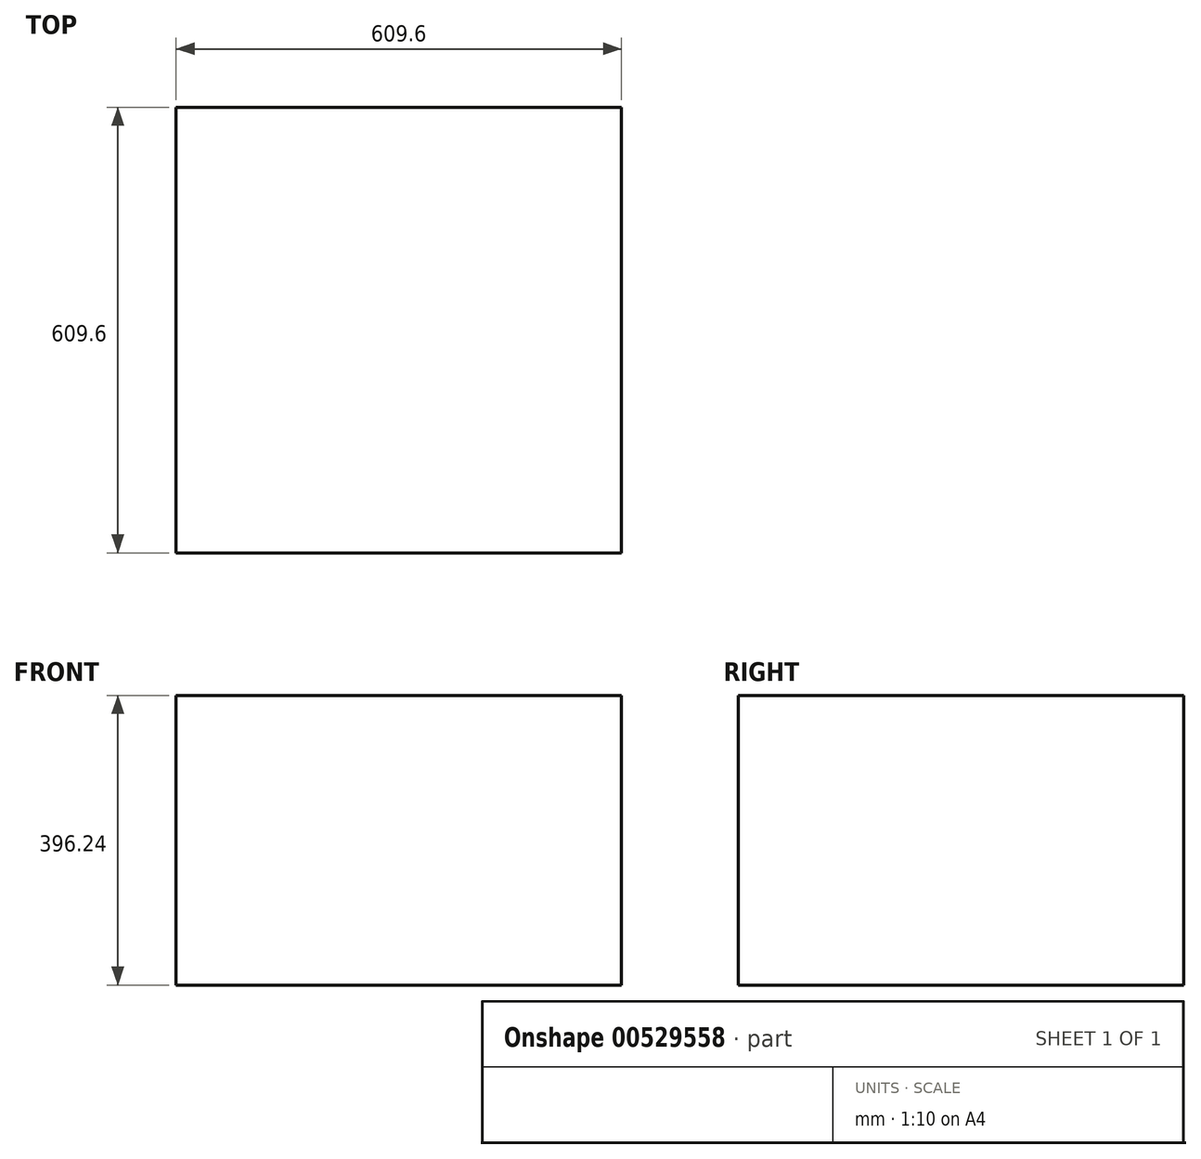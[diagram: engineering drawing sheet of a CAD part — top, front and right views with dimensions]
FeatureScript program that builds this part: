
annotation { "Feature Type Name" : "Feature", "Feature Type Description" : "" }
export const myFeature = defineFeature(function(context is Context, id is Id, definition is map)
    precondition{}
    {
        {
            var Q0;
            Q0=qCreatedBy(makeId("Top.planeOp"),FACE);
            var sketch = newSketch(context, id + "F0", { "sketchPlane" : qUnion([Q0])});
            skLineSegment(sketch, "E0.bottom", {"start": v(-304, 233.03) * mm, "end": v(305.6, 233.03) * mm});
            skLineSegment(sketch, "E0.top", {"start": v(-304, -376.57) * mm, "end": v(305.6, -376.57) * mm});
            skLineSegment(sketch, "E0.left", {"start": v(-304, 233.03) * mm, "end": v(-304, -376.57) * mm});
            skLineSegment(sketch, "E0.right", {"start": v(305.6, 233.03) * mm, "end": v(305.6, -376.57) * mm});
            skSolve(sketch);
        }
        {
            var Q0;
            Q0=makeQuery(id+"F0.imprint","IMPRINT",FACE,{"disambiguationData":[TD([[makeQuery(id+"F0.imprint","IMPRINT",EDGE,{"derivedFrom":sQuery(id+"F0.wireOp",EDGE,"E0.bottom")}),-1.0]])]});
            extrude(context, id + "F1", {"entities" : qUnion([Q0]), "depth" : 396.24 * mm, "offsetDistance" : 30.48 * mm});
        }
    });
